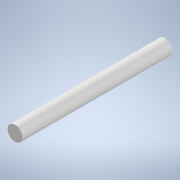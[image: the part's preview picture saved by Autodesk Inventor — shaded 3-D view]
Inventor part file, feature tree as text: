
AUTODESK INVENTOR PART (.ipt)
format: ipt  version: 2020 (Build 240168000, 168)  size: 91,648 bytes
history: native  units: mm
features: extrude x1, sketch x1
ambient origin geometry x8: Origin, YZ Plane, XZ Plane, XY Plane, X Axis, Y Axis, Z Axis, Center Point
bodies: Solid1 (feature_tree)
feature tree (2):
  extrude  "Extrusion1"  Depth=50.0mm TaperAngle=0.0deg
  sketch  "Sketch1"  dims[d0=10.0mm d1=50.0mm d2=0.0mm]
